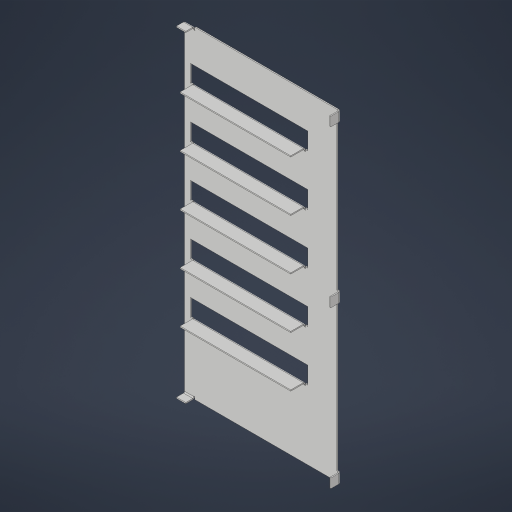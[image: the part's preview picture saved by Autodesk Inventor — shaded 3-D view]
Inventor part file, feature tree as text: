
AUTODESK INVENTOR PART (.ipt)
format: ipt  version: 2023.4 (Build 274418000, 418)  size: 408,064 bytes
history: native  units: in
note: dims shown in document units (in); Inventor stores cm internally (conversion verified against a paired STEP export)
features: sheet_metal_op x12, sketch x6, other x5, pattern_linear x1, extrude x1, projected_geometry x1
ambient origin geometry x8: Origin, YZ Plane, XZ Plane, XY Plane, X Axis, Y Axis, Z Axis, Center Point
bodies: Solid1 (feature_tree)
feature tree (26):
  sheet_metal_op  "Face1"
  sketch  "Sketch2"  dims[d1=35.0in]
  sheet_metal_op  "Face2"
  sheet_metal_op  "Fold1"
  sheet_metal_op  "Fold2"
  sketch  "Sketch3"  dims[d2=0.12in]
  sheet_metal_op  "Fold4"
  pattern_linear  "Rectangular Pattern1"  Spacing1=1.0in  [1 undecoded]
  extrude  "Extrusion1"  Depth=1.0in
  sheet_metal_op  "Flange1"
  sheet_metal_op  "Flange2"
  sketch  "Sketch1"  dims[d0=16.5in]
  other  "Plate1"
  other  "Plate2"
  sheet_metal_op  "Bend1"
  sketch  "Sketch4"  dims[d3=1.25in]
  sketch  "Sketch5"  dims[d4=1.0in]
  other  "Plate3"
  sheet_metal_op  "Bend2"
  sheet_metal_op  "Corner1"
  sketch  "Sketch6"  dims[d5=0.25in d6=1.0in d7=1.0in d8=1.25in d9=1.0in d10=0.25in d11=0.12in d12=0.12in d13=0.06in d14=0.24in d15=0.12in d16=0.12in d17=0.06in d18=0.24in d19=0.12in d20=90.0deg d21=0.12in d22=0.12in d23=0.06in d24=0.24in d25=0.12in d26=90.0deg d27=0.12in d28=5.5in d29=1.5in d30=12.0in d31=1.0in d32=0.375in d33=0.12in d34=0.0in d41=0.12in d42=0.06in d43=0.24in d44=0.12in d45=90.0deg d46=0.12in d47=1.9685in d49=5.5in d50=1.0in d51=0.0in d52=0.12in d53=0.06in d54=0.24in d55=0.12in d56=1.0in d57=0.0in d58=1.0in d59=90.0deg d60=0.12in d61=0.48in d62=0.12in d63=0.12in d64=0.12in d65=0.06in d66=0.24in d67=0.12in d68=1.0in d69=0.0in d70=1.0in d71=90.0deg d72=0.12in d73=0.48in d74=0.12in d75=0.12in]
  other  "Plate4"
  sheet_metal_op  "Bend3"
  sheet_metal_op  "Corner2"
  other  "Cut1"
  projected_geometry  "Project Cut Edges1"
note: 1 required parameter value undecoded (feature->parameter linkage not recoverable at this tier; creation-order binding heuristic only, values carry confidence <= 0.55)
